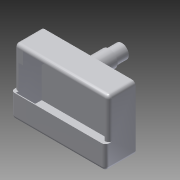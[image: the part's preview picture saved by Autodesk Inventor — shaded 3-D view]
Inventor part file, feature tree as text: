
AUTODESK INVENTOR PART (.ipt)
format: ipt  version: 2014 (Build 180170000, 170)  size: 207,360 bytes
history: native  units: in
note: dims shown in document units (in); Inventor stores cm internally (conversion verified against a paired STEP export)
features: extrude x7, sketch x7, chamfer x3, fillet x3
ambient origin geometry x8: Origin, YZ Plane, XZ Plane, XY Plane, X Axis, Y Axis, Z Axis, Center Point
bodies: Solid1 (feature_tree)
feature tree (20):
  extrude  "Extrusion1"  Depth=0.275in
  extrude  "Extrusion2"  Depth=0.6in
  extrude  "Extrusion3"  Depth=0.36in
  extrude  "Extrusion5"  Depth=0.1in TaperAngle=0.0deg
  extrude  "Extrusion6"  Depth=1.0in
  extrude  "Extrusion7"  Depth=2.7in
  extrude  "Extrusion8"  Depth=0.1in
  chamfer  "Chamfer1"  Distance=1.12in
  chamfer  "Chamfer2"  Distance=0.1in
  chamfer  "Chamfer3"  [1 undecoded]
  fillet  "Fillet1"  Radius=2.46in
  fillet  "Fillet2"  Radius=0.12in
  fillet  "Fillet3"  Radius=0.12in
  sketch  "Sketch1"  dims[d0=0.48in d1=0.275in]
  sketch  "Sketch2"  dims[d2=0.6in d3=0.0in d4=0.4in]
  sketch  "Sketch3"  dims[d5=0.36in d6=0.0in d9=0.3in]
  sketch  "Sketch6"  dims[d10=0.3in d11=0.1in d12=0.0in]
  sketch  "Sketch7"  dims[d13=2.1in d14=1.0in]
  sketch  "Sketch8"  dims[d15=1.1in d51=2.7in]
  sketch  "Sketch9"  dims[d52=1.35in d53=1.35in d54=1.12in d55=0.1in d56=0.0in d57=0.0in d58=2.46in d59=0.12in d60=0.12in d61=0.12in d62=1.0in d63=0.3in d64=0.3in d65=1.1in d66=1.0in d67=0.66in d68=0.0in d69=-0.0in d79=0.3in d80=0.55in d81=0.116in d82=0.3in d83=0.0in d84=0.55in d85=0.1in d86=0.0in d87=0.075in d88=0.25in d89=45.0deg d90=0.25in d91=0.5in d92=45.0deg d93=0.25in d94=0.5in d95=45.0deg d96=0.058in d97=0.1in d98=0.1in]
note: 1 required parameter value undecoded (feature->parameter linkage not recoverable at this tier; creation-order binding heuristic only, values carry confidence <= 0.55)
